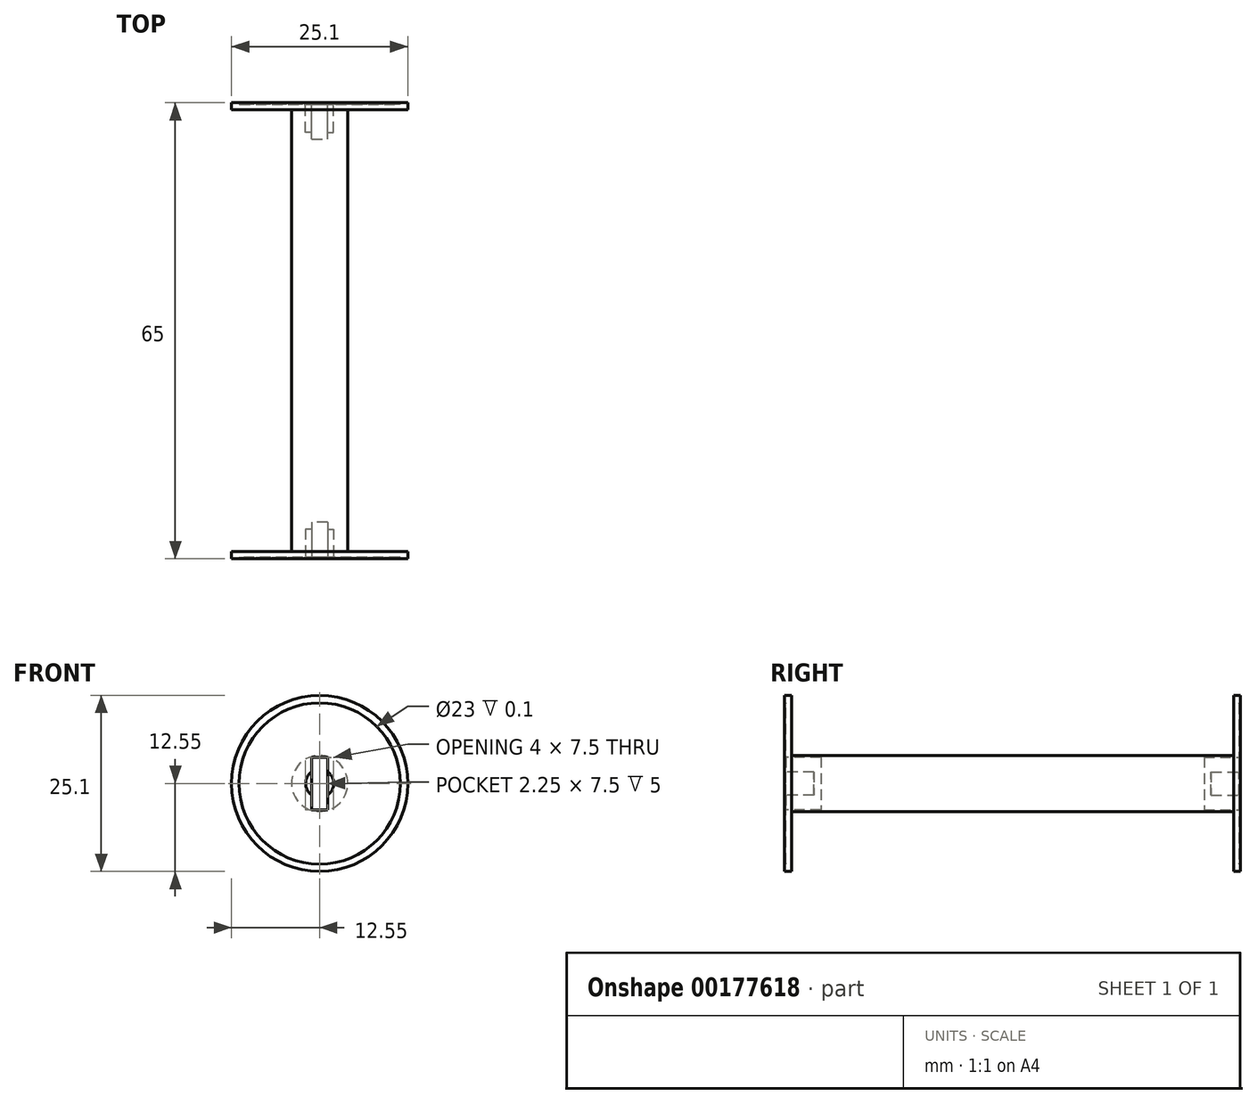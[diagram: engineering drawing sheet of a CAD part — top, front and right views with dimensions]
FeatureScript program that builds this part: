
annotation { "Feature Type Name" : "Feature", "Feature Type Description" : "" }
export const myFeature = defineFeature(function(context is Context, id is Id, definition is map)
    precondition{}
    {
        {
            var Q0;
            Q0=qCreatedBy(makeId("Front.planeOp"),FACE);
            var sketch = newSketch(context, id + "F0", { "sketchPlane" : qUnion([Q0])});
            skCircle(sketch, "E0", {"center": v(0, 0) * mm, "radius": 12.55 * mm});
            skSolve(sketch);
        }
        {
            var Q0;
            Q0=qSketchRegion(id+"F0",true);
            extrude(context, id + "F1", {"entities" : qUnion([Q0]), "depth" : 1 * mm});
        }
        {
            var Q0;
            Q0=makeQuery(id+"F1.opExtrude","CAP_FACE",FACE,{"disambiguationData":[OSD([sQuery(id+"F0.wireOp",EDGE,"E0")])],"isStart":false});
            var sketch = newSketch(context, id + "F2", { "sketchPlane" : qUnion([Q0])});
            skCircle(sketch, "E1", {"center": v(0, 0) * mm, "radius": 4 * mm});
            skSolve(sketch);
        }
        {
            var Q0;
            Q0=qSketchRegion(id+"F2",true);
            extrude(context, id + "F3", {"entities" : qUnion([Q0]), "operationType" : NewBodyOperationType.ADD, "depth" : 63 * mm});
        }
        {
            var Q0;
            Q0=makeQuery(id+"F3.opExtrude","CAP_FACE",FACE,{"disambiguationData":[OSD([sQuery(id+"F2.wireOp",EDGE,"E1")])],"isStart":false});
            var sketch = newSketch(context, id + "F4", { "sketchPlane" : qUnion([Q0])});
            skCircle(sketch, "E2", {"center": v(0, 0) * mm, "radius": 12.55 * mm});
            skSolve(sketch);
        }
        {
            var Q0;
            Q0=qSketchRegion(id+"F4",true);
            extrude(context, id + "F5", {"entities" : qUnion([Q0]), "operationType" : NewBodyOperationType.ADD, "depth" : 1 * mm});
        }
        {
            var Q0;
            Q0=makeQuery(id+"F5.opExtrude","CAP_FACE",FACE,{"disambiguationData":[OSD([sQuery(id+"F4.wireOp",EDGE,"E2")])],"isStart":false});
            var sketch = newSketch(context, id + "F6", { "sketchPlane" : qUnion([Q0])});
            skCircle(sketch, "E3", {"center": v(0, 0) * mm, "radius": 11.5 * mm});
            skSolve(sketch);
        }
        {
            var Q0;
            Q0=qSketchRegion(id+"F6",true);
            extrude(context, id + "F7", {"entities" : qUnion([Q0]), "operationType" : NewBodyOperationType.REMOVE, "oppositeDirection" : true, "depth" : .2 * mm});
        }
        {
            var Q0;
            Q0=makeQuery(id+"F7.boolean.opBoolean","COPY",EDGE,{"derivedFrom":makeQuery(id+"F7.opExtrude","CAP_EDGE",EDGE,{"disambiguationData":[OSD([sQuery(id+"F6.wireOp",EDGE,"E3")])],"isStart":true})});
            var Q1;
            Q1=makeQuery(id+"F7.boolean.opBoolean","COPY",FACE,{"derivedFrom":makeQuery(id+"F7.opExtrude","SWEPT_FACE",FACE,{"disambiguationData":[OSD([sQuery(id+"F6.wireOp",EDGE,"E3")])]})});
            fillet(context, id + "F8", {"entities" : qUnion([Q0, Q1]), "radius" : .1 * mm, "tangentPropagation" : true, "allowEdgeOverflow" : false});
        }
        {
            var Q0;
            Q0=makeQuery(id+"F7.boolean.opBoolean","COPY",FACE,{"derivedFrom":makeQuery(id+"F7.opExtrude","CAP_FACE",FACE,{"disambiguationData":[OSD([sQuery(id+"F6.wireOp",EDGE,"E3")])],"isStart":false})});
            var sketch = newSketch(context, id + "F9", { "sketchPlane" : qUnion([Q0])});
            skCircle(sketch, "E4", {"center": v(0, 0) * mm, "radius": 2 * mm});
            skSolve(sketch);
        }
        {
            var Q0;
            Q0=qSketchRegion(id+"F9",true);
            extrude(context, id + "F10", {"entities" : qUnion([Q0]), "operationType" : NewBodyOperationType.REMOVE, "oppositeDirection" : true, "depth" : 4 * mm});
        }
        {
            var Q0;
            Q0=makeQuery(id+"F7.boolean.opBoolean","COPY",FACE,{"derivedFrom":makeQuery(id+"F7.opExtrude","CAP_FACE",FACE,{"disambiguationData":[OSD([sQuery(id+"F6.wireOp",EDGE,"E3")])],"isStart":false})});
            var sketch = newSketch(context, id + "F11", { "sketchPlane" : qUnion([Q0])});
            skLineSegment(sketch, "E5.bottom", {"start": v(1.13, 3.75) * mm, "end": v(-1.13, 3.75) * mm});
            skLineSegment(sketch, "E5.top", {"start": v(1.13, -3.75) * mm, "end": v(-1.13, -3.75) * mm});
            skLineSegment(sketch, "E5.left", {"start": v(1.13, 3.75) * mm, "end": v(1.13, -3.75) * mm});
            skLineSegment(sketch, "E5.right", {"start": v(-1.13, 3.75) * mm, "end": v(-1.13, -3.75) * mm});
            skPoint(sketch, "E5.middle", {"position": v(0, 0) * mm});
            skSolve(sketch);
        }
        {
            var Q0;
            Q0=qSketchRegion(id+"F11",true);
            extrude(context, id + "F12", {"entities" : qUnion([Q0]), "operationType" : NewBodyOperationType.REMOVE, "oppositeDirection" : true, "depth" : 5 * mm});
        }
        {
            var Q0;
            Q0=makeQuery(id+"F1.opExtrude","CAP_FACE",FACE,{"disambiguationData":[OSD([sQuery(id+"F0.wireOp",EDGE,"E0")])],"isStart":true});
            var sketch = newSketch(context, id + "F13", { "sketchPlane" : qUnion([Q0])});
            skCircle(sketch, "E6", {"center": v(0, 0) * mm, "radius": 11.5 * mm});
            skSolve(sketch);
        }
        {
            var Q0;
            Q0=qSketchRegion(id+"F13",true);
            extrude(context, id + "F14", {"entities" : qUnion([Q0]), "operationType" : NewBodyOperationType.REMOVE, "oppositeDirection" : true, "depth" : .2 * mm});
        }
        {
            var Q0;
            Q0=makeQuery(id+"F14.boolean.opBoolean","COPY",EDGE,{"derivedFrom":makeQuery(id+"F14.opExtrude","CAP_EDGE",EDGE,{"disambiguationData":[OSD([sQuery(id+"F13.wireOp",EDGE,"E6")])],"isStart":true})});
            var Q1;
            Q1=makeQuery(id+"F14.boolean.opBoolean","COPY",EDGE,{"derivedFrom":makeQuery(id+"F14.opExtrude","CAP_EDGE",EDGE,{"disambiguationData":[OSD([sQuery(id+"F13.wireOp",EDGE,"E6")])],"isStart":false})});
            fillet(context, id + "F15", {"entities" : qUnion([Q0, Q1]), "radius" : .1 * mm, "tangentPropagation" : true, "allowEdgeOverflow" : false});
        }
        {
            var Q0;
            Q0=makeQuery(id+"F14.boolean.opBoolean","COPY",FACE,{"derivedFrom":makeQuery(id+"F14.opExtrude","CAP_FACE",FACE,{"disambiguationData":[OSD([sQuery(id+"F13.wireOp",EDGE,"E6")])],"isStart":false})});
            var sketch = newSketch(context, id + "F16", { "sketchPlane" : qUnion([Q0])});
            skCircle(sketch, "E7", {"center": v(0, 0) * mm, "radius": 2 * mm});
            skSolve(sketch);
        }
        {
            var Q0;
            Q0=qSketchRegion(id+"F16",true);
            extrude(context, id + "F17", {"entities" : qUnion([Q0]), "operationType" : NewBodyOperationType.REMOVE, "oppositeDirection" : true, "depth" : 4 * mm});
        }
        {
            var Q0;
            Q0=makeQuery(id+"F14.boolean.opBoolean","COPY",FACE,{"derivedFrom":makeQuery(id+"F14.opExtrude","CAP_FACE",FACE,{"disambiguationData":[OSD([sQuery(id+"F13.wireOp",EDGE,"E6")])],"isStart":false})});
            var sketch = newSketch(context, id + "F18", { "sketchPlane" : qUnion([Q0])});
            skLineSegment(sketch, "E8.bottom", {"start": v(1.12, 3.75) * mm, "end": v(-1.13, 3.75) * mm});
            skLineSegment(sketch, "E8.top", {"start": v(1.13, -3.75) * mm, "end": v(-1.12, -3.75) * mm});
            skLineSegment(sketch, "E8.left", {"start": v(1.12, 3.75) * mm, "end": v(1.13, -3.75) * mm});
            skLineSegment(sketch, "E8.right", {"start": v(-1.13, 3.75) * mm, "end": v(-1.12, -3.75) * mm});
            skPoint(sketch, "E8.middle", {"position": v(0, 0) * mm});
            skSolve(sketch);
        }
        {
            var Q0;
            Q0=qSketchRegion(id+"F18",true);
            extrude(context, id + "F19", {"entities" : qUnion([Q0]), "operationType" : NewBodyOperationType.REMOVE, "oppositeDirection" : true, "depth" : 5 * mm});
        }
    });
